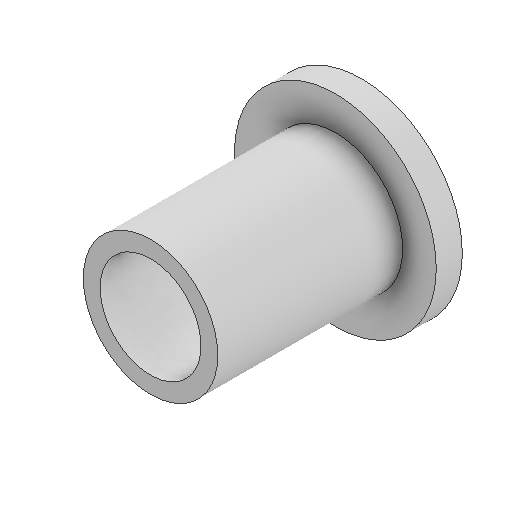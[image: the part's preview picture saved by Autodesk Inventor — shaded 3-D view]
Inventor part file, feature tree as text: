
AUTODESK INVENTOR PART (.ipt)
format: ipt  version: 2025.1 (Build 291241000, 241)  size: 120,320 bytes
history: native  units: mm
features: extrude x2, other x1, sketch x1
ambient origin geometry x8: Origin, YZ Plane, XZ Plane, XY Plane, X Axis, Y Axis, Z Axis, Center Point
bodies: Body1 (feature_tree)
feature tree (4):
  other  "Bryła1"
  sketch  "Szkic1"
  extrude  "Wyciągnięcie proste1"  Depth=3.0mm
  extrude  "Wyciągnięcie proste2"  Depth=4.0mm
